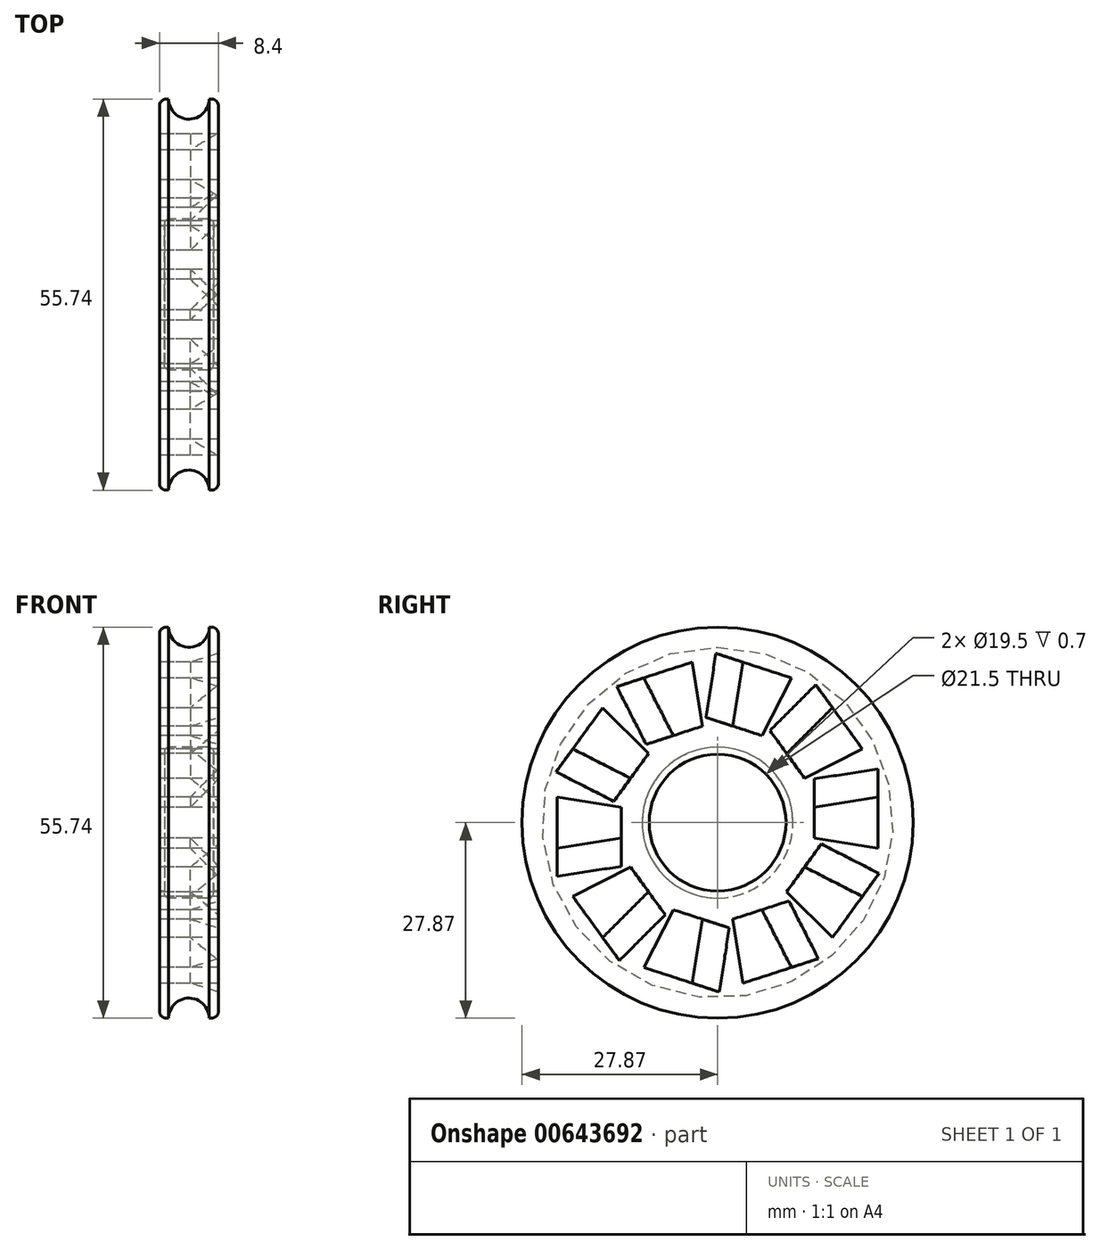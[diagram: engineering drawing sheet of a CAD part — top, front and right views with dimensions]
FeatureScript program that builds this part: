
annotation { "Feature Type Name" : "Feature", "Feature Type Description" : "" }
export const myFeature = defineFeature(function(context is Context, id is Id, definition is map)
    precondition{}
    {
        {
            var Q0;
            Q0=qCreatedBy(makeId("Front.planeOp"),FACE);
            var sketch = newSketch(context, id + "F0", { "sketchPlane" : qUnion([Q0])});
            skLineSegment(sketch, "E0", {"start": v(-37.18, 0) * mm, "end": v(33.4, 0) * mm, "construction": true});
            skLineSegment(sketch, "E1", {"start": v(-9.67, 27.87) * mm, "end": v(-9.67, 9.75) * mm});
            skLineSegment(sketch, "E2", {"start": v(-9.67, 9.75) * mm, "end": v(-8.97, 9.75) * mm});
            skLineSegment(sketch, "E3", {"start": v(-8.97, 9.75) * mm, "end": v(-8.97, 10.75) * mm});
            skLineSegment(sketch, "E4", {"start": v(-8.97, 10.75) * mm, "end": v(-1.97, 10.75) * mm});
            skLineSegment(sketch, "E5", {"start": v(-1.97, 10.75) * mm, "end": v(-1.97, 9.75) * mm});
            skLineSegment(sketch, "E6", {"start": v(-1.97, 9.75) * mm, "end": v(-1.27, 9.75) * mm});
            skLineSegment(sketch, "E7", {"start": v(-1.27, 27.87) * mm, "end": v(-1.27, 9.75) * mm});
            skPoint(sketch, "E8", {"position": v(-8.37, 27.87) * mm});
            skPoint(sketch, "E9", {"position": v(-2.57, 27.87) * mm});
            skArc(sketch, "E10", {"start": v(-8.37, 27.87) * mm, "mid": v(-5.47, 25) * mm, "end": v(-2.57, 27.87) * mm});
            skLineSegment(sketch, "E11", {"start": v(-9.67, 27.87) * mm, "end": v(-8.37, 27.87) * mm});
            skLineSegment(sketch, "E12", {"start": v(-2.57, 27.87) * mm, "end": v(-1.27, 27.87) * mm});
            skLineSegment(sketch, "E13", {"start": v(-5.47, 25) * mm, "end": v(-9.67, 25) * mm, "construction": true});
            skSolve(sketch);
        }
        {
            var Q0;
            Q0 = qSketchRegion(id + "F0", true);
            var Q1;
            Q1=sQuery(id+"F0.wireOp",EDGE,"E0");
            revolve(context, id + "F1", {"entities" : qUnion([Q0]), "axis" : qUnion([Q1]), "revolveType" : RevolveType.FULL});
        }
        {
            var Q0;
            Q0=makeQuery(id+"F1.opRevolve","SWEPT_EDGE",EDGE,{"disambiguationData":[OSD([sQuery(id+"F0.wireOp",EDGE,"E3"),sQuery(id+"F0.wireOp",EDGE,"E4")])]});
            var Q1;
            Q1=makeQuery(id+"F1.opRevolve","SWEPT_EDGE",EDGE,{"disambiguationData":[OSD([sQuery(id+"F0.wireOp",EDGE,"E4"),sQuery(id+"F0.wireOp",EDGE,"E5")])]});
            fillet(context, id + "F2", {"entities" : qUnion([Q0, Q1]), "radius" : .7 * mm, "tangentPropagation" : true, "allowEdgeOverflow" : false});
        }
        {
            var Q0;
            Q0=makeQuery(id+"F1.opRevolve","SWEPT_EDGE",EDGE,{"disambiguationData":[OSD([sQuery(id+"F0.wireOp",EDGE,"E1"),sQuery(id+"F0.wireOp",EDGE,"E11")])]});
            var Q1;
            Q1=makeQuery(id+"F1.opRevolve","SWEPT_EDGE",EDGE,{"disambiguationData":[OSD([sQuery(id+"F0.wireOp",EDGE,"E7"),sQuery(id+"F0.wireOp",EDGE,"E12")])]});
            fillet(context, id + "F3", {"entities" : qUnion([Q0, Q1]), "radius" : 1 * mm, "tangentPropagation" : true, "allowEdgeOverflow" : false});
        }
        {
            var Q0;
            Q0=makeQuery(id+"F1.opRevolve","SWEPT_FACE",FACE,{"disambiguationData":[OSD([sQuery(id+"F0.wireOp",EDGE,"E1")])]});
            var sketch = newSketch(context, id + "F4", { "sketchPlane" : qUnion([Q0])});
            skCircle(sketch, "E14.0", {"center": v(0, 0) * mm, "radius": 9.75 * mm});
            skCircle(sketch, "E15.0", {"center": v(0, 0) * mm, "radius": 26.87 * mm});
            skCircle(sketch, "E16.cCircle", {"center": v(0, 0) * mm, "radius": 22.87 * mm, "construction": true});
            skLineSegment(sketch, "E16.0", {"start": v(-22.87, -3.62) * mm, "end": v(-22.87, 3.62) * mm});
            skLineSegment(sketch, "E16.1", {"start": v(-22.87, 3.62) * mm, "end": v(-20.63, 10.51) * mm});
            skLineSegment(sketch, "E16.2", {"start": v(-20.63, 10.51) * mm, "end": v(-16.37, 16.37) * mm});
            skLineSegment(sketch, "E16.3", {"start": v(-16.37, 16.37) * mm, "end": v(-10.51, 20.63) * mm});
            skLineSegment(sketch, "E16.4", {"start": v(-10.51, 20.63) * mm, "end": v(-3.62, 22.87) * mm});
            skLineSegment(sketch, "E16.5", {"start": v(-3.62, 22.87) * mm, "end": v(3.62, 22.87) * mm});
            skLineSegment(sketch, "E16.6", {"start": v(3.62, 22.87) * mm, "end": v(10.51, 20.63) * mm});
            skLineSegment(sketch, "E16.7", {"start": v(10.51, 20.63) * mm, "end": v(16.37, 16.37) * mm});
            skLineSegment(sketch, "E16.8", {"start": v(16.37, 16.37) * mm, "end": v(20.63, 10.51) * mm});
            skLineSegment(sketch, "E16.9", {"start": v(20.63, 10.51) * mm, "end": v(22.87, 3.62) * mm});
            skLineSegment(sketch, "E16.10", {"start": v(22.87, 3.62) * mm, "end": v(22.87, -3.62) * mm});
            skLineSegment(sketch, "E16.11", {"start": v(22.87, -3.62) * mm, "end": v(20.63, -10.51) * mm});
            skLineSegment(sketch, "E16.12", {"start": v(20.63, -10.51) * mm, "end": v(16.37, -16.37) * mm});
            skLineSegment(sketch, "E16.13", {"start": v(16.37, -16.37) * mm, "end": v(10.51, -20.63) * mm});
            skLineSegment(sketch, "E16.14", {"start": v(10.51, -20.63) * mm, "end": v(3.62, -22.87) * mm});
            skLineSegment(sketch, "E16.15", {"start": v(3.62, -22.87) * mm, "end": v(-3.62, -22.87) * mm});
            skLineSegment(sketch, "E16.16", {"start": v(-3.62, -22.87) * mm, "end": v(-10.51, -20.63) * mm});
            skLineSegment(sketch, "E16.17", {"start": v(-10.51, -20.63) * mm, "end": v(-16.37, -16.37) * mm});
            skLineSegment(sketch, "E16.18", {"start": v(-16.37, -16.37) * mm, "end": v(-20.63, -10.51) * mm});
            skLineSegment(sketch, "E16.19", {"start": v(-20.63, -10.51) * mm, "end": v(-22.87, -3.62) * mm});
            skPoint(sketch, "E16.0.midPoint", {"position": v(-22.87, 0) * mm});
            skCircle(sketch, "E17.cCircle", {"center": v(0, 0) * mm, "radius": 13.75 * mm, "construction": true});
            skLineSegment(sketch, "E17.0", {"start": v(-13.75, -2.18) * mm, "end": v(-13.75, 2.18) * mm});
            skLineSegment(sketch, "E17.1", {"start": v(-13.75, 2.18) * mm, "end": v(-12.4, 6.32) * mm});
            skLineSegment(sketch, "E17.2", {"start": v(-12.4, 6.32) * mm, "end": v(-9.84, 9.84) * mm});
            skLineSegment(sketch, "E17.3", {"start": v(-9.84, 9.84) * mm, "end": v(-6.32, 12.4) * mm});
            skLineSegment(sketch, "E17.4", {"start": v(-6.32, 12.4) * mm, "end": v(-2.18, 13.75) * mm});
            skLineSegment(sketch, "E17.5", {"start": v(-2.18, 13.75) * mm, "end": v(2.18, 13.75) * mm});
            skLineSegment(sketch, "E17.6", {"start": v(2.18, 13.75) * mm, "end": v(6.32, 12.4) * mm});
            skLineSegment(sketch, "E17.7", {"start": v(6.32, 12.4) * mm, "end": v(9.84, 9.84) * mm});
            skLineSegment(sketch, "E17.8", {"start": v(9.84, 9.84) * mm, "end": v(12.4, 6.32) * mm});
            skLineSegment(sketch, "E17.9", {"start": v(12.4, 6.32) * mm, "end": v(13.75, 2.18) * mm});
            skLineSegment(sketch, "E17.10", {"start": v(13.75, 2.18) * mm, "end": v(13.75, -2.18) * mm});
            skLineSegment(sketch, "E17.11", {"start": v(13.75, -2.18) * mm, "end": v(12.4, -6.32) * mm});
            skLineSegment(sketch, "E17.12", {"start": v(12.4, -6.32) * mm, "end": v(9.84, -9.84) * mm});
            skLineSegment(sketch, "E17.13", {"start": v(9.84, -9.84) * mm, "end": v(6.32, -12.4) * mm});
            skLineSegment(sketch, "E17.14", {"start": v(6.32, -12.4) * mm, "end": v(2.18, -13.75) * mm});
            skLineSegment(sketch, "E17.15", {"start": v(2.18, -13.75) * mm, "end": v(-2.18, -13.75) * mm});
            skLineSegment(sketch, "E17.16", {"start": v(-2.18, -13.75) * mm, "end": v(-6.32, -12.4) * mm});
            skLineSegment(sketch, "E17.17", {"start": v(-6.32, -12.4) * mm, "end": v(-9.84, -9.84) * mm});
            skLineSegment(sketch, "E17.18", {"start": v(-9.84, -9.84) * mm, "end": v(-12.4, -6.32) * mm});
            skLineSegment(sketch, "E17.19", {"start": v(-12.4, -6.32) * mm, "end": v(-13.75, -2.18) * mm});
            skPoint(sketch, "E17.0.midPoint", {"position": v(-13.75, 0) * mm});
            skLineSegment(sketch, "E18", {"start": v(3.62, 22.87) * mm, "end": v(2.18, 13.75) * mm});
            skLineSegment(sketch, "E19", {"start": v(10.51, 20.63) * mm, "end": v(6.32, 12.4) * mm});
            skLineSegment(sketch, "E20", {"start": v(16.37, 16.37) * mm, "end": v(9.84, 9.84) * mm});
            skLineSegment(sketch, "E21", {"start": v(20.63, 10.51) * mm, "end": v(12.4, 6.32) * mm});
            skLineSegment(sketch, "E22", {"start": v(22.87, 3.62) * mm, "end": v(13.75, 2.18) * mm});
            skLineSegment(sketch, "E23", {"start": v(22.87, -3.62) * mm, "end": v(13.75, -2.18) * mm});
            skLineSegment(sketch, "E24", {"start": v(20.63, -10.51) * mm, "end": v(12.4, -6.32) * mm});
            skLineSegment(sketch, "E25", {"start": v(16.37, -16.37) * mm, "end": v(9.84, -9.84) * mm});
            skLineSegment(sketch, "E26", {"start": v(10.51, -20.63) * mm, "end": v(6.32, -12.4) * mm});
            skLineSegment(sketch, "E27", {"start": v(3.62, -22.87) * mm, "end": v(2.18, -13.75) * mm});
            skLineSegment(sketch, "E28", {"start": v(-3.62, -22.87) * mm, "end": v(-2.18, -13.75) * mm});
            skLineSegment(sketch, "E29", {"start": v(-10.51, -20.63) * mm, "end": v(-6.32, -12.4) * mm});
            skLineSegment(sketch, "E30", {"start": v(-16.37, -16.37) * mm, "end": v(-9.84, -9.84) * mm});
            skLineSegment(sketch, "E31", {"start": v(-12.4, -6.32) * mm, "end": v(-20.63, -10.51) * mm});
            skLineSegment(sketch, "E32", {"start": v(-13.75, -2.18) * mm, "end": v(-22.87, -3.62) * mm});
            skLineSegment(sketch, "E33", {"start": v(-13.75, 2.18) * mm, "end": v(-22.87, 3.62) * mm});
            skLineSegment(sketch, "E34", {"start": v(-12.4, 6.32) * mm, "end": v(-20.63, 10.51) * mm});
            skLineSegment(sketch, "E35", {"start": v(-9.84, 9.84) * mm, "end": v(-16.37, 16.37) * mm});
            skLineSegment(sketch, "E36", {"start": v(-6.32, 12.4) * mm, "end": v(-10.51, 20.63) * mm});
            skLineSegment(sketch, "E37", {"start": v(-2.18, 13.75) * mm, "end": v(-3.62, 22.87) * mm});
            skSolve(sketch);
        }
        {
            var Q0;
            Q0=makeQuery(id+"F4.imprint","IMPRINT",FACE,{"disambiguationData":[TD([[makeQuery(id+"F4.imprint","IMPRINT",EDGE,{"derivedFrom":sQuery(id+"F4.wireOp",EDGE,"E16.2")}),-1.0]])]});
            var Q1;
            Q1=makeQuery(id+"F4.imprint","IMPRINT",FACE,{"disambiguationData":[TD([[makeQuery(id+"F4.imprint","IMPRINT",EDGE,{"derivedFrom":sQuery(id+"F4.wireOp",EDGE,"E16.4")}),-1.0]])]});
            var Q2;
            Q2=makeQuery(id+"F4.imprint","IMPRINT",FACE,{"disambiguationData":[TD([[makeQuery(id+"F4.imprint","IMPRINT",EDGE,{"derivedFrom":sQuery(id+"F4.wireOp",EDGE,"E16.6")}),-1.0]])]});
            var Q3;
            Q3=makeQuery(id+"F4.imprint","IMPRINT",FACE,{"disambiguationData":[TD([[makeQuery(id+"F4.imprint","IMPRINT",EDGE,{"derivedFrom":sQuery(id+"F4.wireOp",EDGE,"E16.8")}),-1.0]])]});
            var Q4;
            Q4=makeQuery(id+"F4.imprint","IMPRINT",FACE,{"disambiguationData":[TD([[makeQuery(id+"F4.imprint","IMPRINT",EDGE,{"derivedFrom":sQuery(id+"F4.wireOp",EDGE,"E16.10")}),-1.0]])]});
            var Q5;
            Q5=makeQuery(id+"F4.imprint","IMPRINT",FACE,{"disambiguationData":[TD([[makeQuery(id+"F4.imprint","IMPRINT",EDGE,{"derivedFrom":sQuery(id+"F4.wireOp",EDGE,"E16.12")}),-1.0]])]});
            var Q6;
            Q6=makeQuery(id+"F4.imprint","IMPRINT",FACE,{"disambiguationData":[TD([[makeQuery(id+"F4.imprint","IMPRINT",EDGE,{"derivedFrom":sQuery(id+"F4.wireOp",EDGE,"E16.14")}),-1.0]])]});
            var Q7;
            Q7=makeQuery(id+"F4.imprint","IMPRINT",FACE,{"disambiguationData":[TD([[makeQuery(id+"F4.imprint","IMPRINT",EDGE,{"derivedFrom":sQuery(id+"F4.wireOp",EDGE,"E16.16")}),-1.0]])]});
            var Q8;
            Q8=makeQuery(id+"F4.imprint","IMPRINT",FACE,{"disambiguationData":[TD([[makeQuery(id+"F4.imprint","IMPRINT",EDGE,{"derivedFrom":sQuery(id+"F4.wireOp",EDGE,"E16.18")}),-1.0]])]});
            var Q9;
            Q9=makeQuery(id+"F4.imprint","IMPRINT",FACE,{"disambiguationData":[TD([[makeQuery(id+"F4.imprint","IMPRINT",EDGE,{"derivedFrom":sQuery(id+"F4.wireOp",EDGE,"E16.0")}),-1.0]])]});
            extrude(context, id + "F5", {"entities" : qUnion([Q0, Q1, Q2, Q3, Q4, Q5, Q6, Q7, Q8, Q9]), "operationType" : NewBodyOperationType.REMOVE, "oppositeDirection" : true, "depth" : 25 * mm, "offsetDistance" : 25 * mm});
        }
        {
            var Q0;
            Q0=makeQuery(id+"F5.boolean.opBoolean","COPY",EDGE,{"derivedFrom":makeQuery(id+"F5.opExtrude","CAP_EDGE",EDGE,{"disambiguationData":[OSD([sQuery(id+"F4.wireOp",EDGE,"E34")])],"isStart":true})});
            var Q1;
            Q1=makeQuery(id+"F5.boolean.opBoolean","COPY",EDGE,{"derivedFrom":makeQuery(id+"F5.opExtrude","CAP_EDGE",EDGE,{"disambiguationData":[OSD([sQuery(id+"F4.wireOp",EDGE,"E32")])],"isStart":true})});
            var Q2;
            Q2=makeQuery(id+"F5.boolean.opBoolean","COPY",EDGE,{"derivedFrom":makeQuery(id+"F5.opExtrude","CAP_EDGE",EDGE,{"disambiguationData":[OSD([sQuery(id+"F4.wireOp",EDGE,"E30")])],"isStart":true})});
            var Q3;
            Q3=makeQuery(id+"F5.boolean.opBoolean","COPY",EDGE,{"derivedFrom":makeQuery(id+"F5.opExtrude","CAP_EDGE",EDGE,{"disambiguationData":[OSD([sQuery(id+"F4.wireOp",EDGE,"E28")])],"isStart":true})});
            var Q4;
            Q4=makeQuery(id+"F5.boolean.opBoolean","COPY",EDGE,{"derivedFrom":makeQuery(id+"F5.opExtrude","CAP_EDGE",EDGE,{"disambiguationData":[OSD([sQuery(id+"F4.wireOp",EDGE,"E26")])],"isStart":true})});
            var Q5;
            Q5=makeQuery(id+"F5.boolean.opBoolean","COPY",EDGE,{"derivedFrom":makeQuery(id+"F5.opExtrude","CAP_EDGE",EDGE,{"disambiguationData":[OSD([sQuery(id+"F4.wireOp",EDGE,"E24")])],"isStart":true})});
            var Q6;
            Q6=makeQuery(id+"F5.boolean.opBoolean","COPY",EDGE,{"derivedFrom":makeQuery(id+"F5.opExtrude","CAP_EDGE",EDGE,{"disambiguationData":[OSD([sQuery(id+"F4.wireOp",EDGE,"E22")])],"isStart":true})});
            var Q7;
            Q7=makeQuery(id+"F5.boolean.opBoolean","COPY",EDGE,{"derivedFrom":makeQuery(id+"F5.opExtrude","CAP_EDGE",EDGE,{"disambiguationData":[OSD([sQuery(id+"F4.wireOp",EDGE,"E20")])],"isStart":true})});
            var Q8;
            Q8=makeQuery(id+"F5.boolean.opBoolean","COPY",EDGE,{"derivedFrom":makeQuery(id+"F5.opExtrude","CAP_EDGE",EDGE,{"disambiguationData":[OSD([sQuery(id+"F4.wireOp",EDGE,"E18")])],"isStart":true})});
            var Q9;
            Q9=makeQuery(id+"F5.boolean.opBoolean","COPY",EDGE,{"derivedFrom":makeQuery(id+"F5.opExtrude","CAP_EDGE",EDGE,{"disambiguationData":[OSD([sQuery(id+"F4.wireOp",EDGE,"E36")])],"isStart":true})});
            var Q10;
            Q10=makeQuery(id+"F5.boolean.opBoolean","INTERSECT",EDGE,{"derivedFrom":[makeQuery(id+"F1.opRevolve","SWEPT_FACE",FACE,{"disambiguationData":[OSD([sQuery(id+"F0.wireOp",EDGE,"E7")])]}),makeQuery(id+"F5.opExtrude","SWEPT_FACE",FACE,{"disambiguationData":[OSD([sQuery(id+"F4.wireOp",EDGE,"E21")])]})]});
            var Q11;
            Q11=makeQuery(id+"F5.boolean.opBoolean","INTERSECT",EDGE,{"derivedFrom":[makeQuery(id+"F1.opRevolve","SWEPT_FACE",FACE,{"disambiguationData":[OSD([sQuery(id+"F0.wireOp",EDGE,"E7")])]}),makeQuery(id+"F5.opExtrude","SWEPT_FACE",FACE,{"disambiguationData":[OSD([sQuery(id+"F4.wireOp",EDGE,"E23")])]})]});
            var Q12;
            Q12=makeQuery(id+"F5.boolean.opBoolean","INTERSECT",EDGE,{"derivedFrom":[makeQuery(id+"F1.opRevolve","SWEPT_FACE",FACE,{"disambiguationData":[OSD([sQuery(id+"F0.wireOp",EDGE,"E7")])]}),makeQuery(id+"F5.opExtrude","SWEPT_FACE",FACE,{"disambiguationData":[OSD([sQuery(id+"F4.wireOp",EDGE,"E25")])]})]});
            var Q13;
            Q13=makeQuery(id+"F5.boolean.opBoolean","INTERSECT",EDGE,{"derivedFrom":[makeQuery(id+"F1.opRevolve","SWEPT_FACE",FACE,{"disambiguationData":[OSD([sQuery(id+"F0.wireOp",EDGE,"E7")])]}),makeQuery(id+"F5.opExtrude","SWEPT_FACE",FACE,{"disambiguationData":[OSD([sQuery(id+"F4.wireOp",EDGE,"E27")])]})]});
            var Q14;
            Q14=makeQuery(id+"F5.boolean.opBoolean","INTERSECT",EDGE,{"derivedFrom":[makeQuery(id+"F1.opRevolve","SWEPT_FACE",FACE,{"disambiguationData":[OSD([sQuery(id+"F0.wireOp",EDGE,"E7")])]}),makeQuery(id+"F5.opExtrude","SWEPT_FACE",FACE,{"disambiguationData":[OSD([sQuery(id+"F4.wireOp",EDGE,"E29")])]})]});
            var Q15;
            Q15=makeQuery(id+"F5.boolean.opBoolean","INTERSECT",EDGE,{"derivedFrom":[makeQuery(id+"F1.opRevolve","SWEPT_FACE",FACE,{"disambiguationData":[OSD([sQuery(id+"F0.wireOp",EDGE,"E7")])]}),makeQuery(id+"F5.opExtrude","SWEPT_FACE",FACE,{"disambiguationData":[OSD([sQuery(id+"F4.wireOp",EDGE,"E31")])]})]});
            var Q16;
            Q16=makeQuery(id+"F5.boolean.opBoolean","INTERSECT",EDGE,{"derivedFrom":[makeQuery(id+"F1.opRevolve","SWEPT_FACE",FACE,{"disambiguationData":[OSD([sQuery(id+"F0.wireOp",EDGE,"E7")])]}),makeQuery(id+"F5.opExtrude","SWEPT_FACE",FACE,{"disambiguationData":[OSD([sQuery(id+"F4.wireOp",EDGE,"E33")])]})]});
            var Q17;
            Q17=makeQuery(id+"F5.boolean.opBoolean","INTERSECT",EDGE,{"derivedFrom":[makeQuery(id+"F1.opRevolve","SWEPT_FACE",FACE,{"disambiguationData":[OSD([sQuery(id+"F0.wireOp",EDGE,"E7")])]}),makeQuery(id+"F5.opExtrude","SWEPT_FACE",FACE,{"disambiguationData":[OSD([sQuery(id+"F4.wireOp",EDGE,"E35")])]})]});
            var Q18;
            Q18=makeQuery(id+"F5.boolean.opBoolean","INTERSECT",EDGE,{"derivedFrom":[makeQuery(id+"F1.opRevolve","SWEPT_FACE",FACE,{"disambiguationData":[OSD([sQuery(id+"F0.wireOp",EDGE,"E7")])]}),makeQuery(id+"F5.opExtrude","SWEPT_FACE",FACE,{"disambiguationData":[OSD([sQuery(id+"F4.wireOp",EDGE,"E37")])]})]});
            var Q19;
            Q19=makeQuery(id+"F5.boolean.opBoolean","INTERSECT",EDGE,{"derivedFrom":[makeQuery(id+"F1.opRevolve","SWEPT_FACE",FACE,{"disambiguationData":[OSD([sQuery(id+"F0.wireOp",EDGE,"E7")])]}),makeQuery(id+"F5.opExtrude","SWEPT_FACE",FACE,{"disambiguationData":[OSD([sQuery(id+"F4.wireOp",EDGE,"E19")])]})]});
            chamfer(context, id + "F6", {"entities" : qUnion([Q0, Q1, Q2, Q3, Q4, Q5, Q6, Q7, Q8, Q9, Q10, Q11, Q12, Q13, Q14, Q15, Q16, Q17, Q18, Q19]), "width" : 4 * mm, "tangentPropagation" : true});
        }
    });
